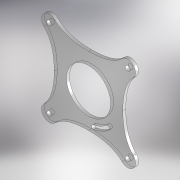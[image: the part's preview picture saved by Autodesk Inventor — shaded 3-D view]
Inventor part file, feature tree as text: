
AUTODESK INVENTOR PART (.ipt)
format: ipt  version: 2018.2 (Build 222227000, 227)  size: 184,832 bytes
history: native  units: mm
features: extrude x2, sketch x1
ambient origin geometry x8: Origin, YZ Plane, XZ Plane, XY Plane, X Axis, Y Axis, Z Axis, Center Point
bodies: Solid1 (feature_tree)
feature tree (3):
  extrude  "Extrusion1"  Depth=10.0mm
  extrude  "Extrusion2"  Depth=10.0mm
  sketch  "Sketch1"  dims[d0=80.0mm d1=80.0mm d2=5.0mm d4=45.0deg d5=5.0mm d6=45.0mm d7=8.0mm d8=3.0mm d9=0.0mm d10=30.0deg d11=4.0mm d12=30.0mm d13=10.0mm d14=0.0mm d15=15.0deg]
